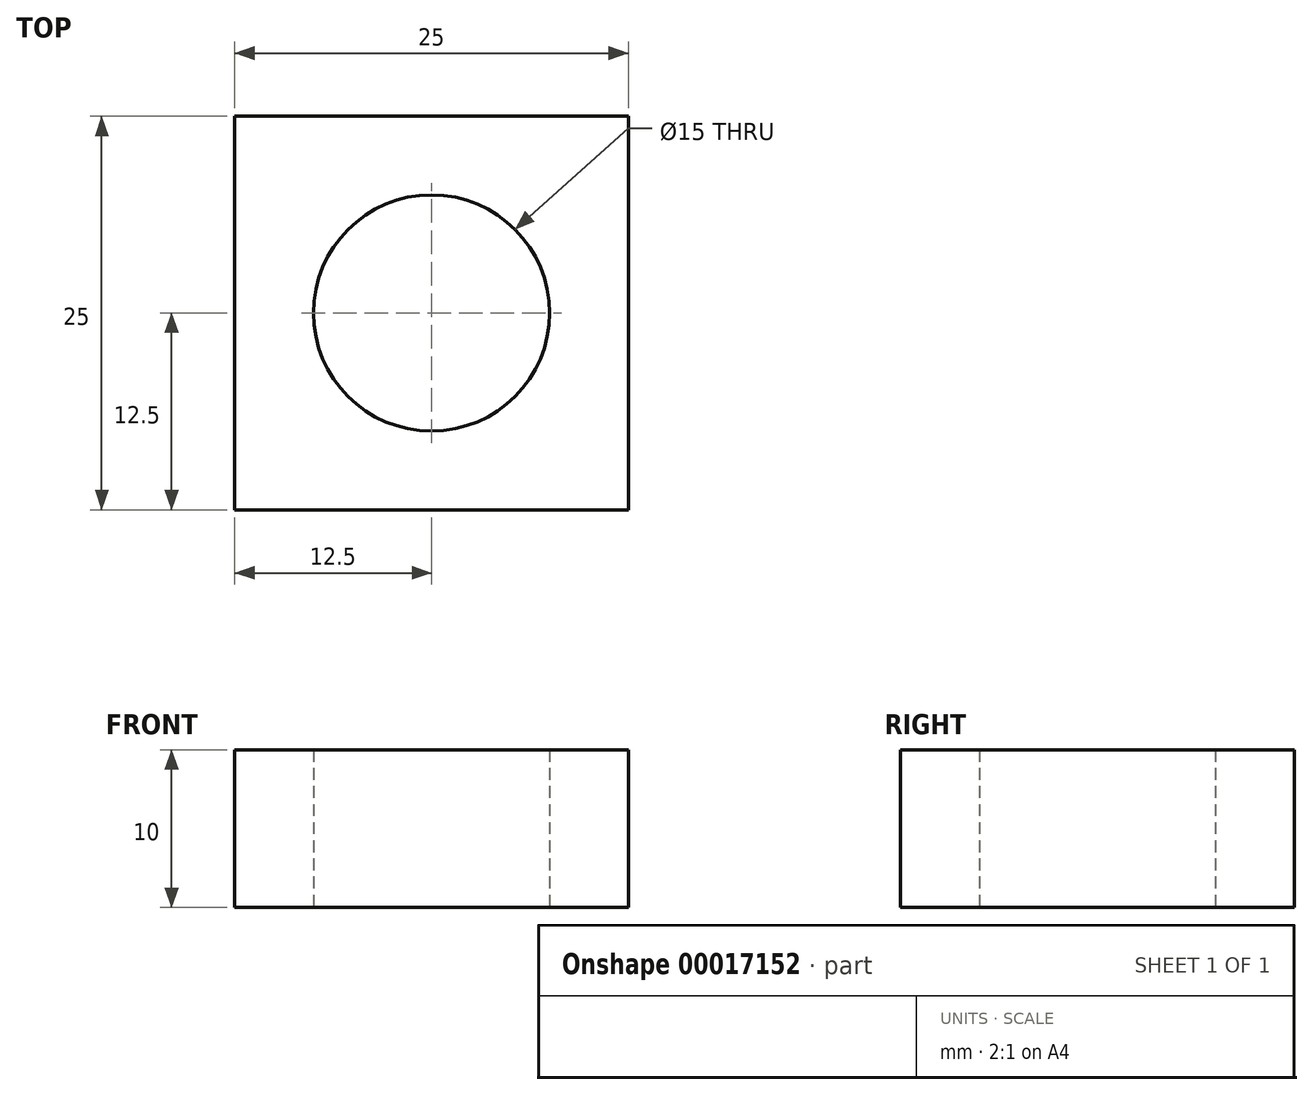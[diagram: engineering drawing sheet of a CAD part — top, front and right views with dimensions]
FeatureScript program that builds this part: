
annotation { "Feature Type Name" : "Feature", "Feature Type Description" : "" }
export const myFeature = defineFeature(function(context is Context, id is Id, definition is map)
    precondition{}
    {
        {
            var Q0;
            Q0=qCreatedBy(makeId("Top.planeOp"),FACE);
            var sketch = newSketch(context, id + "F0", { "sketchPlane" : qUnion([Q0])});
            skLineSegment(sketch, "E0.bottom", {"start": v(-12.5, 12.5) * mm, "end": v(12.5, 12.5) * mm});
            skLineSegment(sketch, "E0.top", {"start": v(-12.5, -12.5) * mm, "end": v(12.5, -12.5) * mm});
            skLineSegment(sketch, "E0.left", {"start": v(-12.5, 12.5) * mm, "end": v(-12.5, -12.5) * mm});
            skLineSegment(sketch, "E0.right", {"start": v(12.5, 12.5) * mm, "end": v(12.5, -12.5) * mm});
            skCircle(sketch, "E1", {"center": v(0, 0) * mm, "radius": 7.5 * mm});
            skSolve(sketch);
        }
        {
            var Q0;
            Q0=makeQuery(id+"F0.imprint","IMPRINT",FACE,{"disambiguationData":[TD([[makeQuery(id+"F0.imprint","IMPRINT",EDGE,{"derivedFrom":sQuery(id+"F0.wireOp",EDGE,"E0.bottom")}),-1.0]])]});
            extrude(context, id + "F1", {"entities" : qUnion([Q0]), "depth" : 10 * mm});
        }
    });
